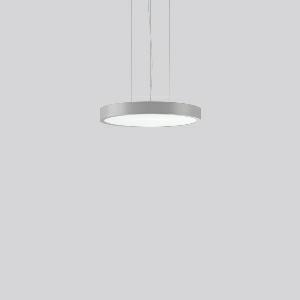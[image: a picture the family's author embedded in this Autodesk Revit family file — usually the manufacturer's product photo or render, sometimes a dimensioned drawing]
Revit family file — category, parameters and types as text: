
# Revit family: triona_round_p_312421_004_1_730_6b1c
name_source: partatom
category: Lighting Fixtures
units: mm (PartAtom-declared; Revit-internal decimal feet)

## family parameters
Cut with Voids When Loaded = No
Host = Face
Light Source = No
Part Type = Normal
Room Calculation Point = No
Round Connector Dimension = Use Diameter
Shared = No

## types (1)
- TRIONA round P (1 x LED Modul 840, 4900 lm, 4000)
    Apparent Load = 48 VA
    CIE Flux Codes = 49 80 96 100 100
    Color Rendering = 80
    Color Temperature = 4000
    Default Elevation = 1800 mm
    Description = Series: TRIONA round
Decorative round LED pendant-mounted surface luminaire. Flat, seamless frame: aluminium extrusion profile, powder coated. Cover made of sheet steel, powder-coated. Canopy made of aluminium, powder-coated. Light emission through a diffuser: plastic, opal. Lightguide and diffuser made of non-yellowing plastic (PMMA). Lateral light emission (RZB SIDELITE technology) for above-average homogeneous light distribution. 3-point steel cable suspension, steplessly adjustable. Easy installation with transparent, adjustable pendant cable and canopy with magnetic fixing. Driver integrated. 
Colour: silver, matt (approx. RAL 9006)
Diameter: 461 mm
Height: 52 mm
Suspension length: 500-1200 mm
Lamp: LED
Socket: without socket
Colour temperature: 4000K
Colour rendering index (CRI): 80
System power: 48 W
Rated luminous flux: 4900 lm
Luminous efficiency: 102 lm/W
Control gear: Dimmable Bluetooth converter
Protection class: I
Type of protection: IP 20
    Height = 52 mm  [stored 0.170604 ft]
    Lamp = 1 x LED Modul 840
    Lamp Light Flux = 4900 lm
    Lamp count = 1
    Length = 461 mm
    Lifetime = 50000 h
    Luminous efficacy = 102 lm/W
    Manufacturer = RZB
    ModVariant = No
    Model = 312421.004.1.730
    Mounting Place = Ceiling
    Mounting Type = Pendant
    Number of Poles = 1
    OnlyDefault = Yes
    Power Factor = 1
    Product Name = TRIONA round P
    Product group = Pendant modular luminaires
    ProductGroupID = 906
    Protection Class = Protection class I
    Protection Degree = IP 20
    RLX_Detail_Level = 1
    RLX_Emergency_Light_Flux = 0 lm
    RLX_Emergency_Type = 0
    RLX_Emergency_Type_DB = No
    RlxData = <blob elided: 25965 chars, md5=b7c53b8c>
    Socket = socket
    Standby Power = 0 W
    System Light Flux = 4900 lm
    System Power = 48 W
    Type Comments = Product without accessories
    Type Image = 312422.004.jpg
    URL = http://relux.com
    VarID = ---
    Voltage = 230 V
    Voltage Range = 220-240 V
    Weight = 0.00 kg
    Width = 0 mm  [stored 0 ft]

note: [stored X ft] marks values corroborated as IEEE doubles in the binary element streams (Revit-internal decimal feet)

## geometry (parser evidence)
native form markers: Blend x4, Sweep x11
no freeform markers — native parametric forms only
